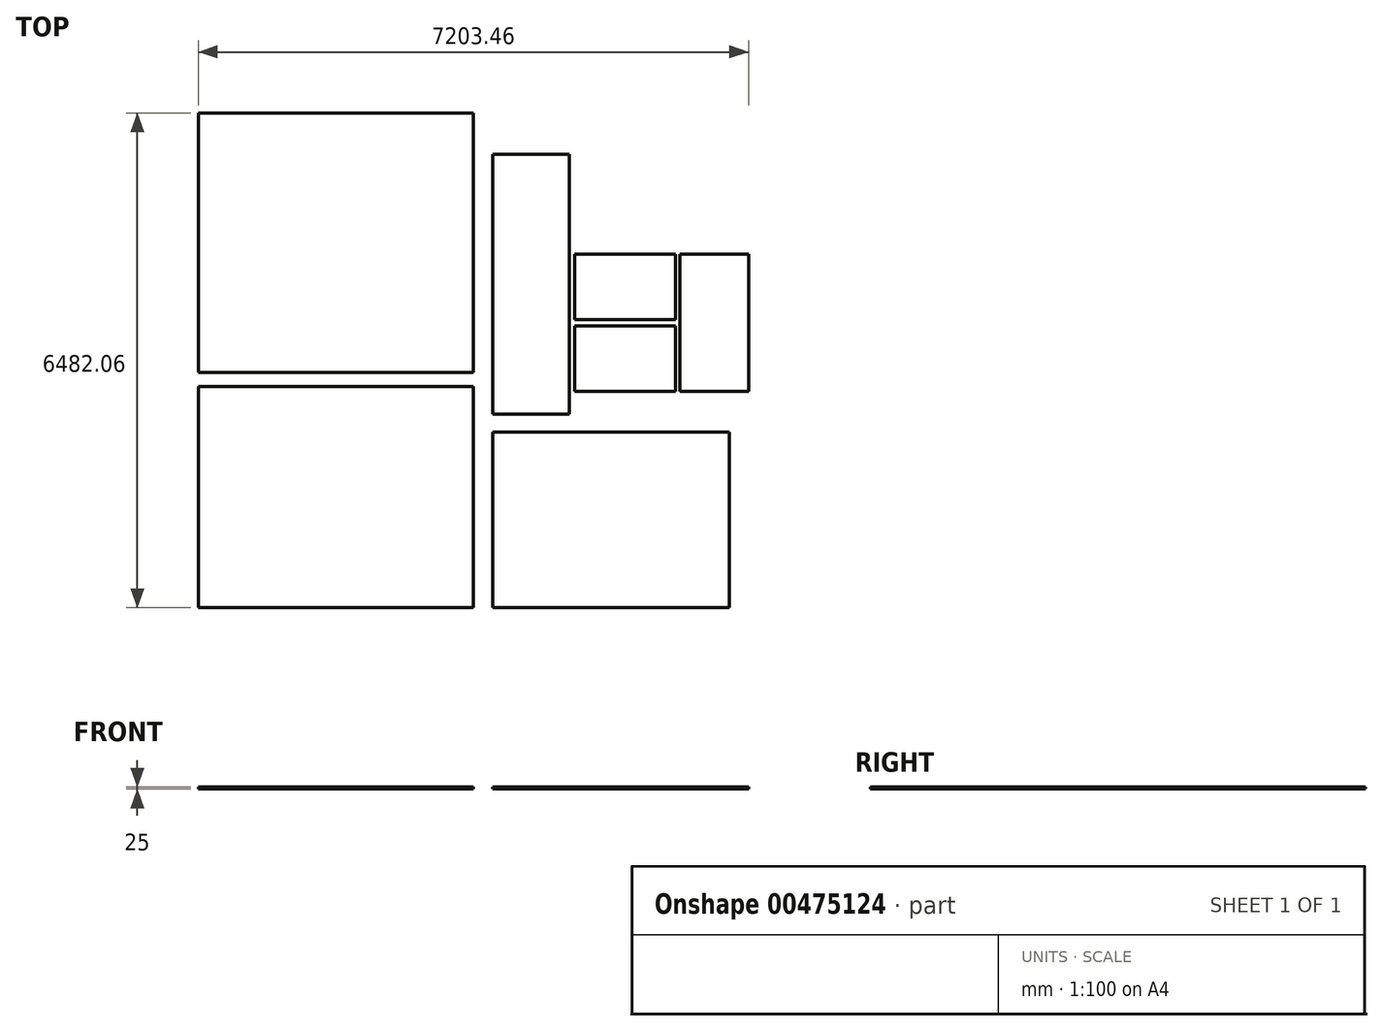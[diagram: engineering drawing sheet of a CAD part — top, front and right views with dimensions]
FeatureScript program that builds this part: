
annotation { "Feature Type Name" : "Feature", "Feature Type Description" : "" }
export const myFeature = defineFeature(function(context is Context, id is Id, definition is map)
    precondition{}
    {
        {
            var Q0;
            Q0=qCreatedBy(makeId("Top.planeOp"),FACE);
            var sketch = newSketch(context, id + "F0", { "sketchPlane" : qUnion([Q0])});
            skLineSegment(sketch, "E0.bottom", {"start": v(-3295.25, 4312.85) * mm, "end": v(304.75, 4312.85) * mm});
            skLineSegment(sketch, "E0.top", {"start": v(-3295.25, 912.85) * mm, "end": v(304.75, 912.85) * mm});
            skLineSegment(sketch, "E0.left", {"start": v(-3295.25, 4312.85) * mm, "end": v(-3295.25, 912.85) * mm});
            skLineSegment(sketch, "E0.right", {"start": v(304.75, 4312.85) * mm, "end": v(304.75, 912.85) * mm});
            skLineSegment(sketch, "E1.bottom", {"start": v(-3295.25, 730.79) * mm, "end": v(304.75, 730.79) * mm});
            skLineSegment(sketch, "E1.top", {"start": v(-3295.25, -2169.21) * mm, "end": v(304.75, -2169.21) * mm});
            skLineSegment(sketch, "E1.left", {"start": v(-3295.25, 730.79) * mm, "end": v(-3295.25, -2169.21) * mm});
            skLineSegment(sketch, "E1.right", {"start": v(304.75, 730.79) * mm, "end": v(304.75, -2169.21) * mm});
            skLineSegment(sketch, "E2.bottom", {"start": v(559.97, 130.79) * mm, "end": v(3659.97, 130.79) * mm});
            skLineSegment(sketch, "E2.top", {"start": v(559.97, -2169.21) * mm, "end": v(3659.97, -2169.21) * mm});
            skLineSegment(sketch, "E2.left", {"start": v(559.97, 130.79) * mm, "end": v(559.97, -2169.21) * mm});
            skLineSegment(sketch, "E2.right", {"start": v(3659.97, 130.79) * mm, "end": v(3659.97, -2169.21) * mm});
            skLineSegment(sketch, "E3.bottom", {"start": v(559.97, 3767.78) * mm, "end": v(1559.97, 3767.78) * mm});
            skLineSegment(sketch, "E3.top", {"start": v(559.97, 367.78) * mm, "end": v(1559.97, 367.78) * mm});
            skLineSegment(sketch, "E3.left", {"start": v(559.97, 3767.78) * mm, "end": v(559.97, 367.78) * mm});
            skLineSegment(sketch, "E3.right", {"start": v(1559.97, 3767.78) * mm, "end": v(1559.97, 367.78) * mm});
            skLineSegment(sketch, "E4.bottom", {"start": v(1634.56, 2462.9) * mm, "end": v(2954.56, 2462.9) * mm});
            skLineSegment(sketch, "E4.top", {"start": v(1634.56, 1602.9) * mm, "end": v(2954.56, 1602.9) * mm});
            skLineSegment(sketch, "E4.left", {"start": v(1634.56, 2462.9) * mm, "end": v(1634.56, 1602.9) * mm});
            skLineSegment(sketch, "E4.right", {"start": v(2954.56, 2462.9) * mm, "end": v(2954.56, 1602.9) * mm});
            skLineSegment(sketch, "E5.bottom", {"start": v(3008.2, 2462.9) * mm, "end": v(3908.2, 2462.9) * mm});
            skLineSegment(sketch, "E5.top", {"start": v(3008.2, 662.9) * mm, "end": v(3908.2, 662.9) * mm});
            skLineSegment(sketch, "E5.left", {"start": v(3008.2, 2462.9) * mm, "end": v(3008.2, 662.9) * mm});
            skLineSegment(sketch, "E5.right", {"start": v(3908.2, 2462.9) * mm, "end": v(3908.2, 662.9) * mm});
            skLineSegment(sketch, "E6.bottom", {"start": v(1634.56, 1522.9) * mm, "end": v(2954.56, 1522.9) * mm});
            skLineSegment(sketch, "E6.top", {"start": v(1634.56, 662.9) * mm, "end": v(2954.56, 662.9) * mm});
            skLineSegment(sketch, "E6.left", {"start": v(1634.56, 1522.9) * mm, "end": v(1634.56, 662.9) * mm});
            skLineSegment(sketch, "E6.right", {"start": v(2954.56, 1522.9) * mm, "end": v(2954.56, 662.9) * mm});
            skSolve(sketch);
        }
        {
            var Q0;
            Q0=makeQuery(id+"F0.imprint","IMPRINT",FACE,{"disambiguationData":[TD([[makeQuery(id+"F0.imprint","IMPRINT",EDGE,{"derivedFrom":sQuery(id+"F0.wireOp",EDGE,"E0.bottom")}),-1.0]])]});
            var Q1;
            Q1=makeQuery(id+"F0.imprint","IMPRINT",FACE,{"disambiguationData":[TD([[makeQuery(id+"F0.imprint","IMPRINT",EDGE,{"derivedFrom":sQuery(id+"F0.wireOp",EDGE,"E1.bottom")}),-1.0]])]});
            var Q2;
            Q2=makeQuery(id+"F0.imprint","IMPRINT",FACE,{"disambiguationData":[TD([[makeQuery(id+"F0.imprint","IMPRINT",EDGE,{"derivedFrom":sQuery(id+"F0.wireOp",EDGE,"E3.bottom")}),-1.0]])]});
            var Q3;
            Q3=makeQuery(id+"F0.imprint","IMPRINT",FACE,{"disambiguationData":[TD([[makeQuery(id+"F0.imprint","IMPRINT",EDGE,{"derivedFrom":sQuery(id+"F0.wireOp",EDGE,"E2.bottom")}),-1.0]])]});
            var Q4;
            Q4=makeQuery(id+"F0.imprint","IMPRINT",FACE,{"disambiguationData":[TD([[makeQuery(id+"F0.imprint","IMPRINT",EDGE,{"derivedFrom":sQuery(id+"F0.wireOp",EDGE,"E4.bottom")}),-1.0]])]});
            var Q5;
            Q5=makeQuery(id+"F0.imprint","IMPRINT",FACE,{"disambiguationData":[TD([[makeQuery(id+"F0.imprint","IMPRINT",EDGE,{"derivedFrom":sQuery(id+"F0.wireOp",EDGE,"E6.bottom")}),-1.0]])]});
            var Q6;
            Q6=makeQuery(id+"F0.imprint","IMPRINT",FACE,{"disambiguationData":[TD([[makeQuery(id+"F0.imprint","IMPRINT",EDGE,{"derivedFrom":sQuery(id+"F0.wireOp",EDGE,"E5.bottom")}),-1.0]])]});
            extrude(context, id + "F1", {"entities" : qUnion([Q0, Q1, Q2, Q3, Q4, Q5, Q6]), "depth" : 25 * mm, "offsetDistance" : 25 * mm});
        }
    });
